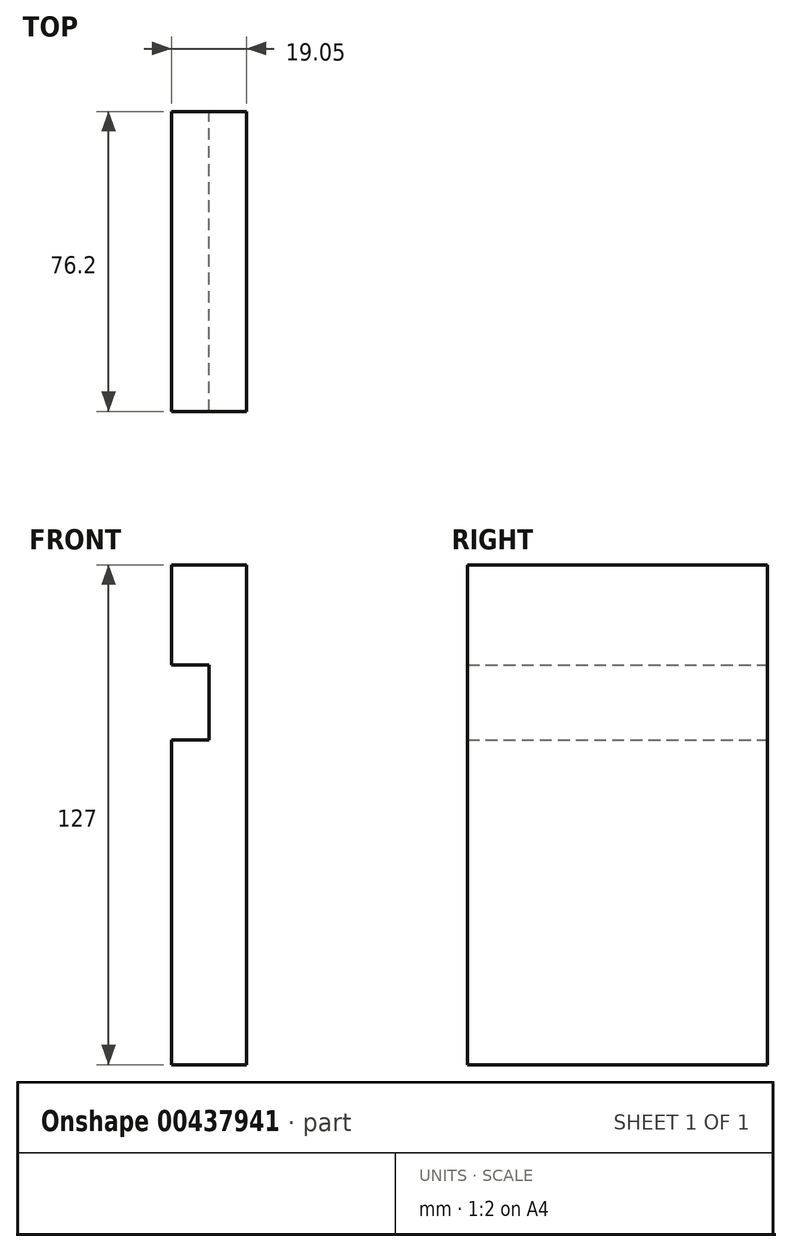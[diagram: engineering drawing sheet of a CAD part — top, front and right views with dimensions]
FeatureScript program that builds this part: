
annotation { "Feature Type Name" : "Feature", "Feature Type Description" : "" }
export const myFeature = defineFeature(function(context is Context, id is Id, definition is map)
    precondition{}
    {
        {
            var Q0;
            Q0=qCreatedBy(makeId("Front.planeOp"),FACE);
            var sketch = newSketch(context, id + "F0", { "sketchPlane" : qUnion([Q0])});
            skLineSegment(sketch, "E0", {"start": v(0, -77.74) * mm, "end": v(0, 49.26) * mm});
            skLineSegment(sketch, "E1", {"start": v(0, 49.26) * mm, "end": v(-19.05, 49.26) * mm});
            skLineSegment(sketch, "E2", {"start": v(-19.05, 49.26) * mm, "end": v(-19.05, 23.86) * mm});
            skLineSegment(sketch, "E3", {"start": v(-19.05, 23.86) * mm, "end": v(-9.52, 23.86) * mm});
            skLineSegment(sketch, "E4", {"start": v(-9.52, 23.86) * mm, "end": v(-9.52, 4.8) * mm});
            skLineSegment(sketch, "E5", {"start": v(-9.52, 4.8) * mm, "end": v(-19.05, 4.8) * mm});
            skLineSegment(sketch, "E6", {"start": v(0, -77.74) * mm, "end": v(-19.05, -77.74) * mm});
            skLineSegment(sketch, "E7", {"start": v(-19.05, -77.74) * mm, "end": v(-19.05, 4.8) * mm});
            skSolve(sketch);
        }
        {
            var Q0;
            Q0=makeQuery(id+"F0.imprint","IMPRINT",FACE,{"disambiguationData":[TD([[makeQuery(id+"F0.imprint","IMPRINT",EDGE,{"derivedFrom":sQuery(id+"F0.wireOp",EDGE,"E0")}),1.0]])]});
            extrude(context, id + "F1", {"entities" : qUnion([Q0]), "depth" : 76.2 * mm});
        }
    });
